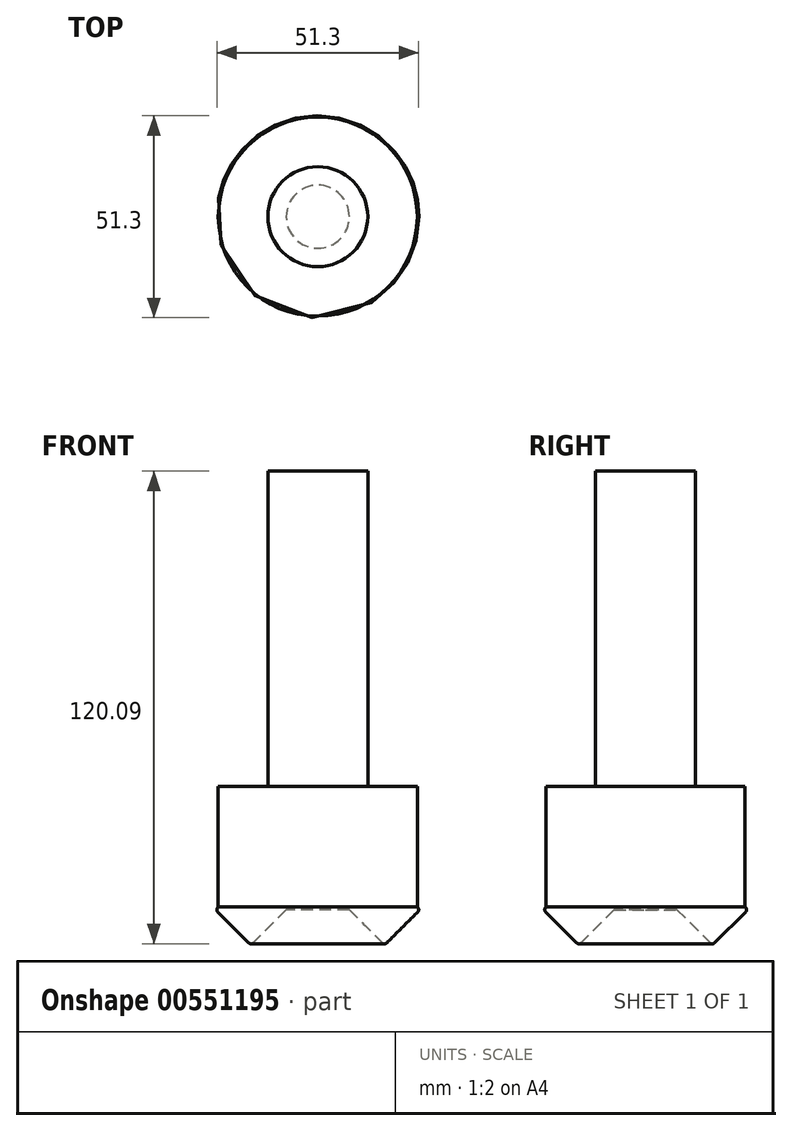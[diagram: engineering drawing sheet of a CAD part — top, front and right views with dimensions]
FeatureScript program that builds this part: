
annotation { "Feature Type Name" : "Feature", "Feature Type Description" : "" }
export const myFeature = defineFeature(function(context is Context, id is Id, definition is map)
    precondition{}
    {
        {
            var Q0;
            Q0=qCreatedBy(makeId("Right.planeOp"),FACE);
            var sketch = newSketch(context, id + "F0", { "sketchPlane" : qUnion([Q0])});
            skLineSegment(sketch, "E0", {"start": v(-25.27, 40) * mm, "end": v(0, 40) * mm});
            skLineSegment(sketch, "E1", {"start": v(0, 40) * mm, "end": v(0, 8.66) * mm});
            skLineSegment(sketch, "E2", {"start": v(0, 8.66) * mm, "end": v(-8, 8.66) * mm});
            skLineSegment(sketch, "E3", {"start": v(-8, 8.66) * mm, "end": v(-16.45, 0.22) * mm});
            skLineSegment(sketch, "E4", {"start": v(-17.53, 0.22) * mm, "end": v(-25.43, 8.13) * mm});
            skLineSegment(sketch, "E5", {"start": v(-25.43, 9.2) * mm, "end": v(-25.27, 9.36) * mm});
            skPoint(sketch, "E6.visualSharp", {"position": v(-16.99, -0.32) * mm});
            skArc(sketch, "E6.filletArc", {"start": v(-17.53, 0.22) * mm, "mid": v(-16.99, 0) * mm, "end": v(-16.45, 0.22) * mm});
            skPoint(sketch, "E7.visualSharp", {"position": v(-25.97, 8.66) * mm});
            skArc(sketch, "E7.filletArc", {"start": v(-25.43, 9.2) * mm, "mid": v(-25.65, 8.66) * mm, "end": v(-25.43, 8.13) * mm});
            skLineSegment(sketch, "E8", {"start": v(-25.27, 40) * mm, "end": v(-25.27, 9.36) * mm});
            skSolve(sketch);
        }
        {
            var Q0;
            Q0=qSketchRegion(id+"F0",true);
            var Q1;
            Q1=sQuery(id+"F0.wireOp",EDGE,"E1");
            revolve(context, id + "F1", {"entities" : qUnion([Q0]), "axis" : qUnion([Q1]), "revolveType" : RevolveType.FULL});
        }
        {
            var Q0;
            Q0=makeQuery(id+"F1.opRevolve","SWEPT_FACE",FACE,{"disambiguationData":[OSD([sQuery(id+"F0.wireOp",EDGE,"E0")])]});
            var sketch = newSketch(context, id + "F2", { "sketchPlane" : qUnion([Q0])});
            skCircle(sketch, "E9", {"center": v(0, 0) * mm, "radius": 12.7 * mm});
            skSolve(sketch);
        }
        {
            var Q0;
            Q0=qSketchRegion(id+"F2",true);
            extrude(context, id + "F3", {"entities" : qUnion([Q0]), "operationType" : NewBodyOperationType.ADD, "depth" : 80.1 * mm, "offsetDistance" : 25.4 * mm});
        }
    });
